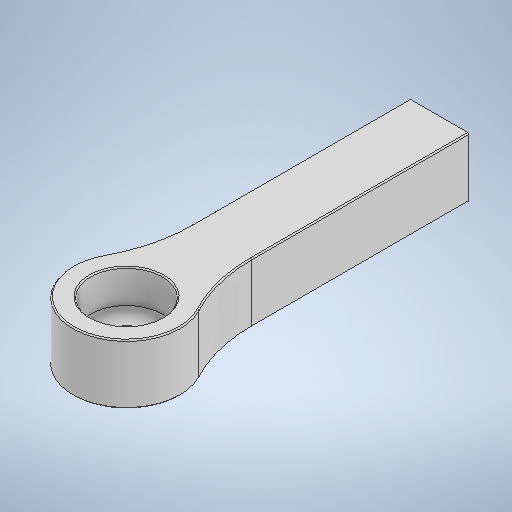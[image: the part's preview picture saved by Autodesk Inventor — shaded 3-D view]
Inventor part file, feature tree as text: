
AUTODESK INVENTOR PART (.ipt)
format: ipt  version: 2025.1 (Build 291241000, 241)  size: 306,176 bytes
history: native  units: mm
features: extrude x5, sketch x5, fillet x3
ambient origin geometry x8: Origin, YZ Plane, XZ Plane, XY Plane, X Axis, Y Axis, Z Axis, Center Point
bodies: Body1 (feature_tree)
feature tree (13):
  extrude  "Extrusion1"  TaperAngle=0.0deg  [1 undecoded]
  extrude  "Extrusion2"  Depth=10.0mm TaperAngle=0.0deg
  fillet  "Rundung1"  Radius=5.0mm
  fillet  "Rundung2"  Radius=5.0mm
  extrude  "Extrusion3"  Depth=5.6mm TaperAngle=0.0deg
  fillet  "Rundung3"  Radius=0.2mm
  extrude  "Extrusion4"  Depth=0.2mm
  extrude  "Extrusion5"  Depth=0.2mm
  sketch  "Skizze1"  dims[d1=18.0mm d4=25.0mm d7=0.0mm d8=52.5mm d9=0.0mm]
  sketch  "Skizze4"  dims[d10=0.0mm d11=10.0mm d12=0.0mm d20=5.0mm d21=5.0mm]
  sketch  "Skizze5"  dims[d22=12.1mm d23=5.6mm d24=0.0mm d25=0.2mm]
  sketch  "Skizze6"  dims[d26=0.2mm d27=3.5mm]
  sketch  "Skizze7"  dims[d28=4.2mm d29=0.0mm d30=0.2mm d31=3.5mm d32=5.0mm d33=5.0mm d34=4.0mm d35=0.0mm d36=8.0mm d37=3.0mm d38=0.0mm]
note: 1 required parameter value undecoded (feature->parameter linkage not recoverable at this tier; creation-order binding heuristic only, values carry confidence <= 0.55)
